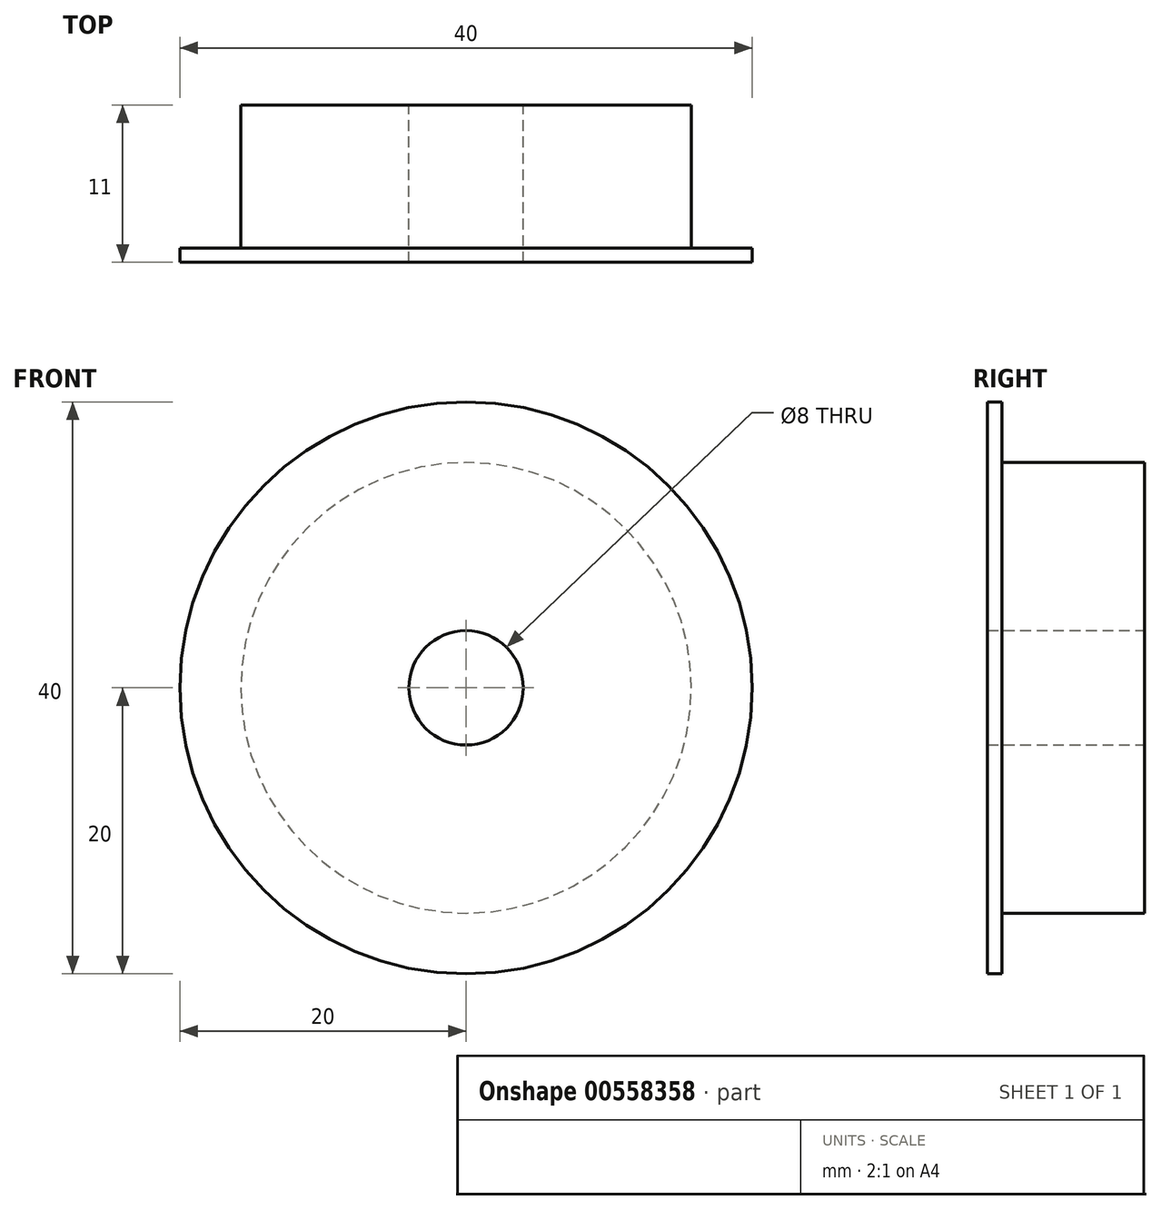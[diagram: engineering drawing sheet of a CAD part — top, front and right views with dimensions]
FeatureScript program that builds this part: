
annotation { "Feature Type Name" : "Feature", "Feature Type Description" : "" }
export const myFeature = defineFeature(function(context is Context, id is Id, definition is map)
    precondition{}
    {
        {
            var Q0;
            Q0=qCreatedBy(makeId("Front.planeOp"),FACE);
            var sketch = newSketch(context, id + "F0", { "sketchPlane" : qUnion([Q0])});
            skCircle(sketch, "E0", {"center": v(0, 0) * mm, "radius": 20 * mm});
            skCircle(sketch, "E1", {"center": v(0, 0) * mm, "radius": 15.75 * mm});
            skCircle(sketch, "E2", {"center": v(0, 0) * mm, "radius": 4 * mm});
            skSolve(sketch);
        }
        {
            var Q0;
            Q0=makeQuery(id+"F0.imprint","IMPRINT",FACE,{"disambiguationData":[TD([[makeQuery(id+"F0.imprint","IMPRINT",EDGE,{"derivedFrom":sQuery(id+"F0.wireOp",EDGE,"E0")}),1.0]])]});
            var Q1;
            Q1=makeQuery(id+"F0.imprint","IMPRINT",FACE,{"disambiguationData":[TD([[makeQuery(id+"F0.imprint","IMPRINT",EDGE,{"derivedFrom":sQuery(id+"F0.wireOp",EDGE,"uPNKFI7G-mird-nQEl-giv2-BQIDvNKOsM9f")}),1.0]])]});
            var Q2;
            Q2=makeQuery(id+"F0.imprint","IMPRINT",FACE,{"disambiguationData":[TD([[makeQuery(id+"F0.imprint","IMPRINT",EDGE,{"derivedFrom":sQuery(id+"F0.wireOp",EDGE,"E1")}),1.0]])]});
            extrude(context, id + "F1", {"entities" : qUnion([Q0, Q1, Q2]), "depth" : 1 * mm, "offsetDistance" : 25 * mm});
        }
        {
            var Q0;
            Q0=makeQuery(id+"F0.imprint","IMPRINT",FACE,{"disambiguationData":[TD([[makeQuery(id+"F0.imprint","IMPRINT",EDGE,{"derivedFrom":sQuery(id+"F0.wireOp",EDGE,"E1")}),1.0]])]});
            extrude(context, id + "F2", {"entities" : qUnion([Q0]), "operationType" : NewBodyOperationType.ADD, "oppositeDirection" : true, "depth" : 10 * mm, "offsetDistance" : 25 * mm});
        }
    });
